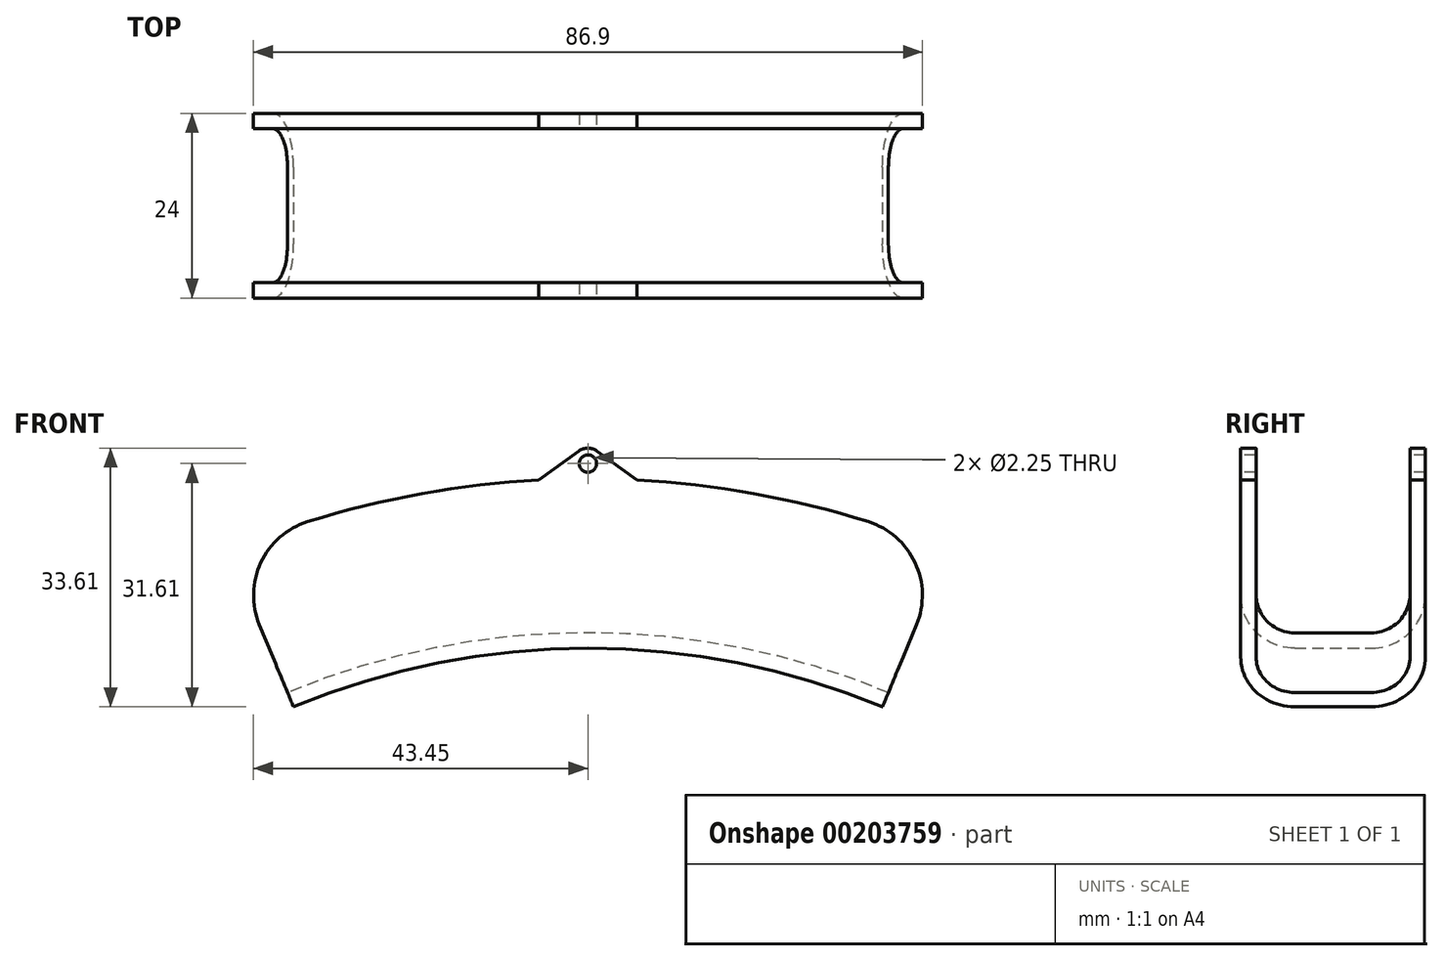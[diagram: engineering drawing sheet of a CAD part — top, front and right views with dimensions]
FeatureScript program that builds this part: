
annotation { "Feature Type Name" : "Feature", "Feature Type Description" : "" }
export const myFeature = defineFeature(function(context is Context, id is Id, definition is map)
    precondition{}
    {
        {
            var Q0;
            Q0=qCreatedBy(makeId("Right.planeOp"),FACE);
            var sketch = newSketch(context, id + "F0", { "sketchPlane" : qUnion([Q0])});
            skLineSegment(sketch, "E0.bottom", {"start": v(10, -10) * mm, "end": v(-10, -10) * mm});
            skLineSegment(sketch, "E0.left", {"start": v(10, -10) * mm, "end": v(10, 10) * mm});
            skLineSegment(sketch, "E0.right", {"start": v(-10, -10) * mm, "end": v(-10, 10) * mm});
            skPoint(sketch, "E0.middle", {"position": v(0, 0) * mm});
            skLineSegment(sketch, "E1.0", {"start": v(-12, -12) * mm, "end": v(-12, 10) * mm});
            skLineSegment(sketch, "E1.1", {"start": v(12, -12) * mm, "end": v(-12, -12) * mm});
            skLineSegment(sketch, "E1.2", {"start": v(12, -12) * mm, "end": v(12, 10) * mm});
            skLineSegment(sketch, "E2", {"start": v(-12, 10) * mm, "end": v(-10, 10) * mm});
            skLineSegment(sketch, "E3", {"start": v(10, 10) * mm, "end": v(12, 10) * mm});
            skLineSegment(sketch, "E4", {"start": v(0, -12) * mm, "end": v(0, -112) * mm, "construction": true});
            skLineSegment(sketch, "E5", {"start": v(0, -112) * mm, "end": v(-73.83, -112) * mm, "construction": true});
            skSolve(sketch);
        }
        {
            var Q0;
            Q0=makeQuery(id+"F0.imprint","IMPRINT",FACE,{"disambiguationData":[TD([[makeQuery(id+"F0.imprint","IMPRINT",EDGE,{"derivedFrom":sQuery(id+"F0.wireOp",EDGE,"E0.bottom")}),1.0]])]});
            var Q1;
            Q1=sQuery(id+"F0.wireOp",EDGE,"E5");
            var Q2;
            Q2=sQuery(id+"F0.wireOp",EDGE,"E5");
            revolve(context, id + "F1", {"entities" : qUnion([Q0]), "surfaceEntities" : qUnion([Q1]), "axis" : qUnion([Q2]), "revolveType" : RevolveType.SYMMETRIC, "angle" : 45 * degree});
        }
        {
            var Q0;
            Q0=makeQuery(id+"F1.opRevolve","SWEPT_FACE",FACE,{"disambiguationData":[OSD([sQuery(id+"F0.wireOp",EDGE,"E1.0")])]});
            var sketch = newSketch(context, id + "F2", { "sketchPlane" : qUnion([Q0])});
            skLineSegment(sketch, "E6", {"start": v(0, 10) * mm, "end": v(0, 12) * mm, "construction": true});
            skPoint(sketch, "E6.endSnap0", {"position": v(0, 10) * mm});
            skArc(sketch, "E7", {"start": v(1.18, 13.62) * mm, "mid": v(0, 14) * mm, "end": v(-1.18, 13.62) * mm});
            skLineSegment(sketch, "E8", {"start": v(-1.18, 13.62) * mm, "end": v(-8.13, 8.55) * mm});
            skLineSegment(sketch, "E9.MirrorCS", {"start": v(1.18, 13.62) * mm, "end": v(8.13, 8.55) * mm});
            skLineSegment(sketch, "E10", {"start": v(-8.13, 8.55) * mm, "end": v(8.13, 8.55) * mm});
            skCircle(sketch, "E11", {"center": v(0, 12) * mm, "radius": 1.13 * mm});
            skSolve(sketch);
        }
        {
            var Q0;
            {var subQ0=sQuery(id+"F2.wireOp",EDGE,"E7");Q0=makeQuery(id+"F2.imprint","IMPRINT",FACE,{"disambiguationData":[TD([[makeQuery(id+"F2.imprint","IMPRINT",EDGE,{"derivedFrom":subQ0}),1.0]])]});}
            extrude(context, id + "F3", {"entities" : qUnion([Q0]), "operationType" : NewBodyOperationType.ADD, "oppositeDirection" : true, "depth" : 24 * mm});
        }
        {
            var Q0;
            Q0=qCreatedBy(makeId("Right.planeOp"),FACE);
            var sketch = newSketch(context, id + "F4", { "sketchPlane" : qUnion([Q0])});
            skLineSegment(sketch, "E12", {"start": v(0, 0) * mm, "end": v(-10, 0) * mm});
            skLineSegment(sketch, "E13", {"start": v(-10, 0) * mm, "end": v(-10, 19.67) * mm});
            skLineSegment(sketch, "E14", {"start": v(-10, 19.67) * mm, "end": v(10, 19.67) * mm});
            skLineSegment(sketch, "E15", {"start": v(10, 19.67) * mm, "end": v(10, 0) * mm});
            skLineSegment(sketch, "E16", {"start": v(0, 0) * mm, "end": v(10, 0) * mm});
            skSolve(sketch);
        }
        {
            var Q0;
            Q0=makeQuery(id+"F4.imprint","IMPRINT",FACE,{"disambiguationData":[TD([[makeQuery(id+"F4.imprint","IMPRINT",EDGE,{"derivedFrom":sQuery(id+"F4.wireOp",EDGE,"E12")}),-1.0]])]});
            extrude(context, id + "F5", {"entities" : qUnion([Q0]), "operationType" : NewBodyOperationType.REMOVE, "oppositeDirection" : true, "depth" : 20 * mm, "symmetric" : true});
        }
        {
            var Q0;
            Q0=makeQuery(id+"F1.opRevolve","CAP_EDGE",EDGE,{"disambiguationData":[OSD([sQuery(id+"F0.wireOp",EDGE,"E3")])],"isStart":false});
            var Q1;
            Q1=makeQuery(id+"F1.opRevolve","CAP_EDGE",EDGE,{"disambiguationData":[OSD([sQuery(id+"F0.wireOp",EDGE,"E2")])],"isStart":false});
            var Q2;
            Q2=makeQuery(id+"F1.opRevolve","CAP_EDGE",EDGE,{"disambiguationData":[OSD([sQuery(id+"F0.wireOp",EDGE,"E2")])],"isStart":true});
            var Q3;
            Q3=makeQuery(id+"F1.opRevolve","CAP_EDGE",EDGE,{"disambiguationData":[OSD([sQuery(id+"F0.wireOp",EDGE,"E3")])],"isStart":true});
            fillet(context, id + "F6", {"entities" : qUnion([Q0, Q1, Q2, Q3]), "radius" : 10 * mm, "tangentPropagation" : true, "allowEdgeOverflow" : false});
        }
        {
            var Q0;
            Q0=makeQuery(id+"F1.opRevolve","SWEPT_EDGE",EDGE,{"disambiguationData":[OSD([sQuery(id+"F0.wireOp",EDGE,"E0.bottom"),sQuery(id+"F0.wireOp",EDGE,"E0.left")])]});
            var Q1;
            Q1=makeQuery(id+"F1.opRevolve","SWEPT_EDGE",EDGE,{"disambiguationData":[OSD([sQuery(id+"F0.wireOp",EDGE,"E0.bottom"),sQuery(id+"F0.wireOp",EDGE,"E0.right")])]});
            fillet(context, id + "F7", {"entities" : qUnion([Q0, Q1]), "radius" : 5 * mm, "tangentPropagation" : true, "allowEdgeOverflow" : false});
        }
        {
            var Q0;
            Q0=makeQuery(id+"F1.opRevolve","SWEPT_EDGE",EDGE,{"disambiguationData":[OSD([sQuery(id+"F0.wireOp",EDGE,"E1.1"),sQuery(id+"F0.wireOp",EDGE,"E1.2")])]});
            var Q1;
            Q1=makeQuery(id+"F1.opRevolve","SWEPT_EDGE",EDGE,{"disambiguationData":[OSD([sQuery(id+"F0.wireOp",EDGE,"E1.0"),sQuery(id+"F0.wireOp",EDGE,"E1.1")])]});
            fillet(context, id + "F8", {"entities" : qUnion([Q0, Q1]), "radius" : 7 * mm, "tangentPropagation" : true, "allowEdgeOverflow" : false});
        }
    });
